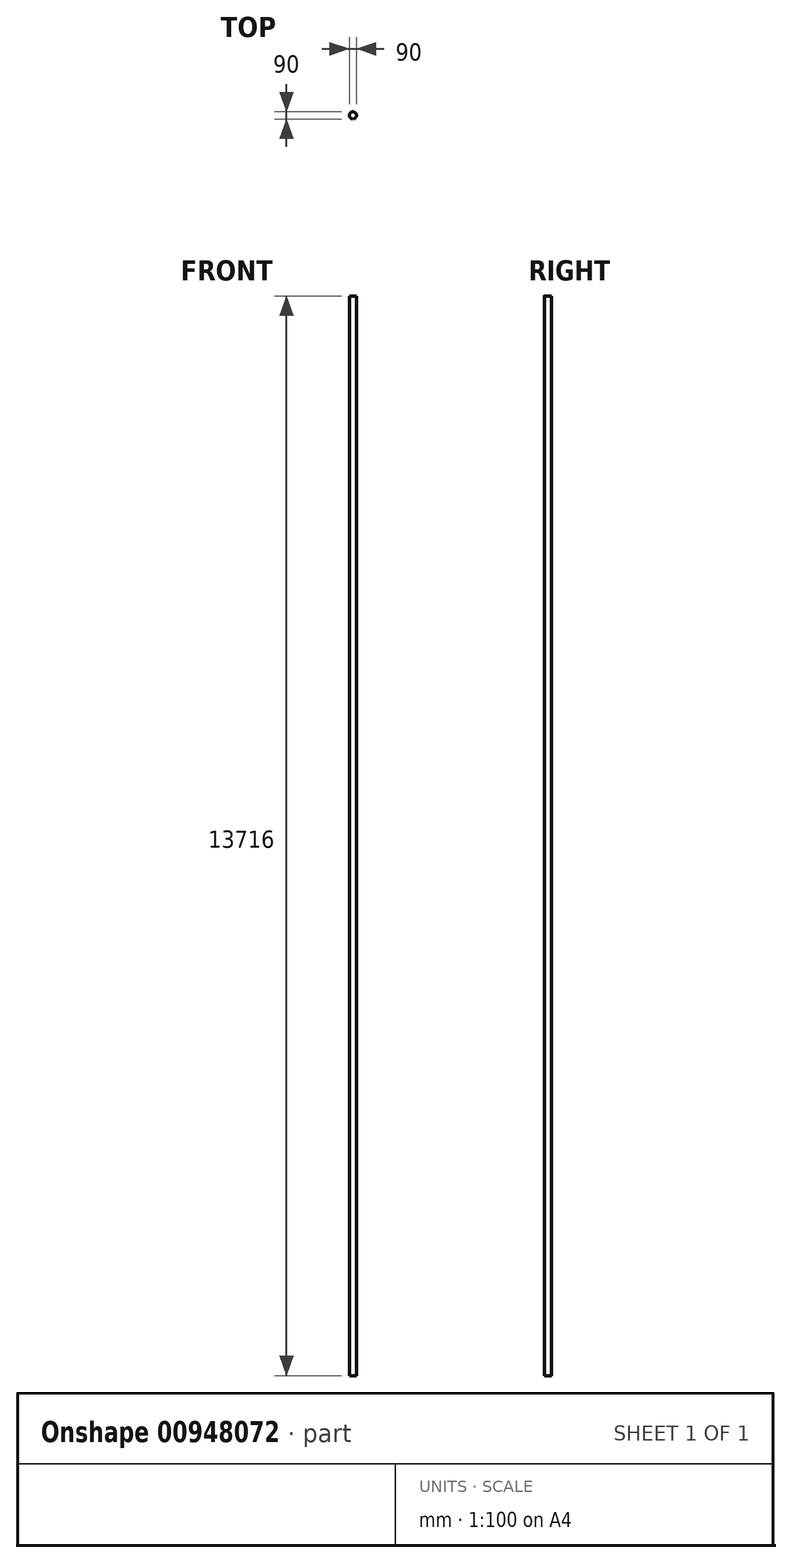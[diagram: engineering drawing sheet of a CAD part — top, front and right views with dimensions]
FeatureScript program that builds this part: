
annotation { "Feature Type Name" : "Feature", "Feature Type Description" : "" }
export const myFeature = defineFeature(function(context is Context, id is Id, definition is map)
    precondition{}
    {
        {
            var Q0;
            Q0=qCreatedBy(makeId("Top.planeOp"),FACE);
            var sketch = newSketch(context, id + "F0", { "sketchPlane" : qUnion([Q0])});
            skCircle(sketch, "E0", {"center": v(0, 0) * mm, "radius": 45 * mm});
            skSolve(sketch);
        }
        {
            var Q0;
            Q0=makeQuery(id+"F0.imprint","IMPRINT",FACE,{"disambiguationData":[TD([[makeQuery(id+"F0.imprint","IMPRINT",EDGE,{"derivedFrom":sQuery(id+"F0.wireOp",EDGE,"E0")}),1.0]])]});
            extrude(context, id + "F1", {"entities" : qUnion([Q0]), "depth" : 13716 * mm, "offsetDistance" : 25 * mm});
        }
    });
